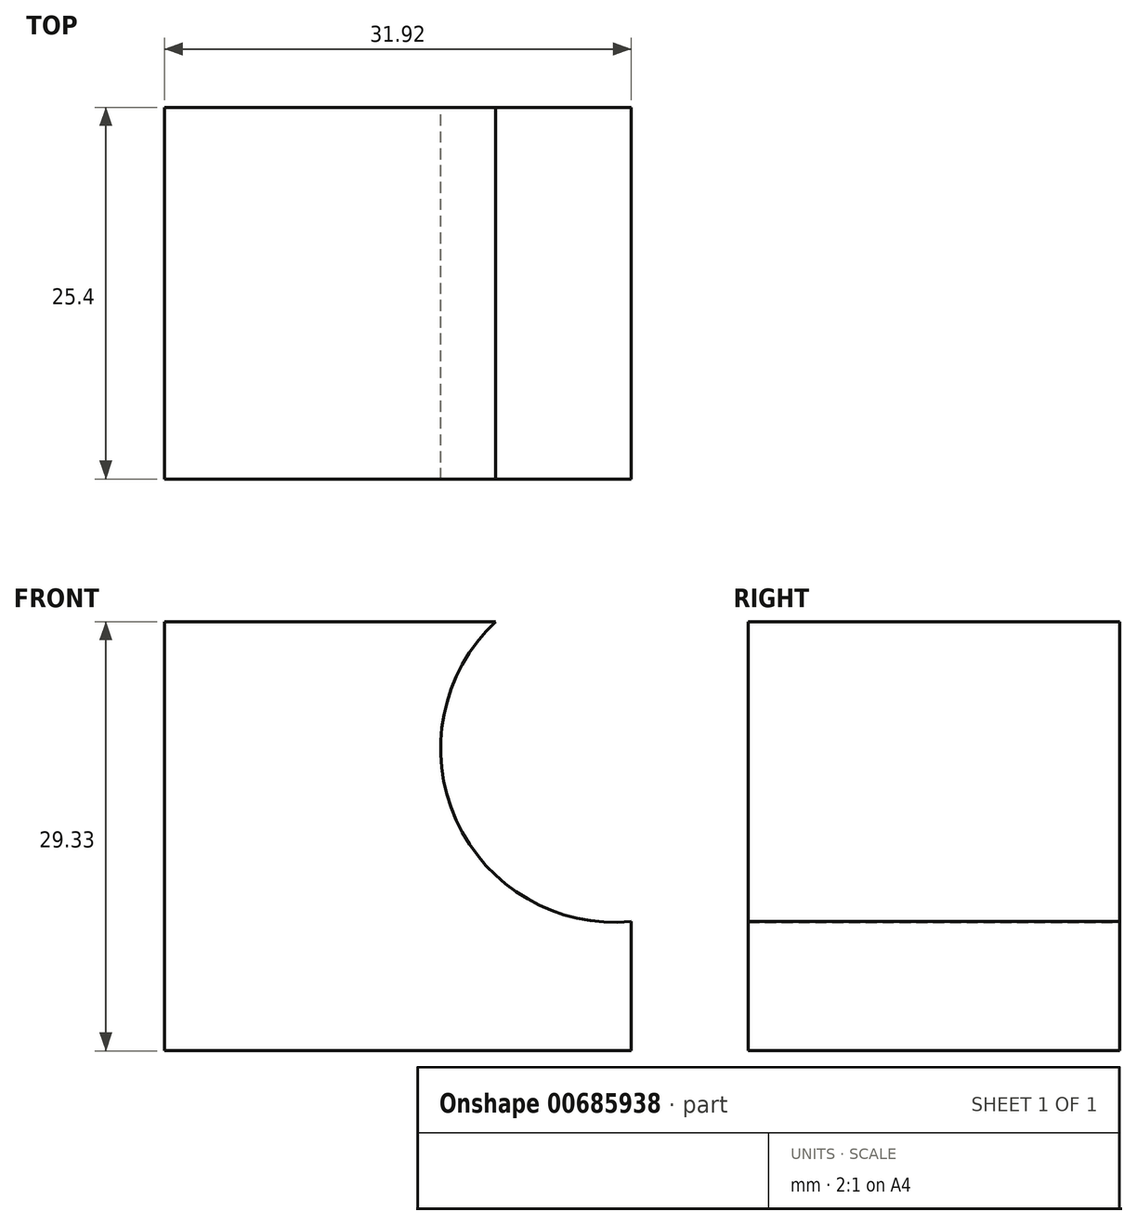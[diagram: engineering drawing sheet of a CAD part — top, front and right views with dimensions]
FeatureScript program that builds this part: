
annotation { "Feature Type Name" : "Feature", "Feature Type Description" : "" }
export const myFeature = defineFeature(function(context is Context, id is Id, definition is map)
    precondition{}
    {
        {
            var Q0;
            Q0=qCreatedBy(makeId("Front.planeOp"),FACE);
            var sketch = newSketch(context, id + "F0", { "sketchPlane" : qUnion([Q0])});
            skLineSegment(sketch, "E0.bottom", {"start": v(-51.87, 44.53) * mm, "end": v(-29.22, 44.53) * mm});
            skLineSegment(sketch, "E0.top", {"start": v(-51.87, 15.2) * mm, "end": v(-19.95, 15.2) * mm});
            skLineSegment(sketch, "E0.left", {"start": v(-51.87, 44.53) * mm, "end": v(-51.87, 15.2) * mm});
            skLineSegment(sketch, "E0.right", {"start": v(-19.95, 24.05) * mm, "end": v(-19.95, 15.2) * mm});
            skArc(sketch, "E1", {"start": v(-29.22, 44.53) * mm, "mid": v(-31.92, 30.97) * mm, "end": v(-19.95, 24.05) * mm});
            skSolve(sketch);
        }
        {
            var Q0;
            Q0=makeQuery(id+"F0.imprint","IMPRINT",FACE,{"disambiguationData":[TD([[makeQuery(id+"F0.imprint","IMPRINT",EDGE,{"derivedFrom":sQuery(id+"F0.wireOp",EDGE,"E0.bottom")}),-1.0]])]});
            extrude(context, id + "F1", {"entities" : qUnion([Q0]), "depth" : 25.4 * mm, "offsetDistance" : 25.4 * mm});
        }
    });
